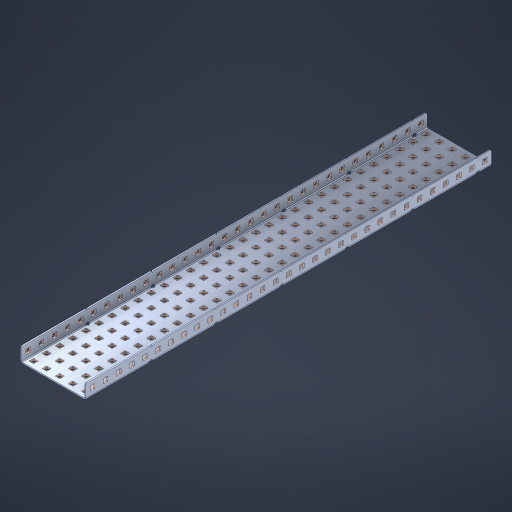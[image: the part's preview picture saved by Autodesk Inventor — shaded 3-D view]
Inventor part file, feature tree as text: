
AUTODESK INVENTOR PART (.ipt)
format: ipt  version: 2023 (Build 270158000, 158)  size: 2,308,096 bytes
history: native  units: in
note: dims shown in document units (in); Inventor stores cm internally (conversion verified against a paired STEP export)
features: other x222, extrude x216, sheet_metal_op x10, sketch x8, mirror x1, pattern_linear x1, chamfer x1
ambient origin geometry x8: Origin, YZ Plane, XZ Plane, XY Plane, X Axis, Y Axis, Z Axis, Center Point
bodies: Solid1 (feature_tree), Body (feature_tree)
feature tree (459):
  other  "Flange Pattern Plane"
  sheet_metal_op  "Flange Pattern"
  sheet_metal_op  "Body Pattern"
  other  "Arc Length"
  mirror  "Notch Mirror"
  pattern_linear  "Notch Pattern"  Spacing1=0.1875in  [1 undecoded]
  chamfer  "End Chamfer"
  extrude  "Half Cut"  Depth=0.0469in
  sketch  "Sketch1"  dims[d0=2.5in]
  other  "Plate1"
  sketch  "Sketch2"  dims[d1=15.5in]
  other  "Plate2"
  sheet_metal_op  "Bend1"
  sheet_metal_op  "Corner1"
  sketch  "Sketch3"  dims[d2=0.0469in]
  other  "Flange Pattern Sketch"
  sketch  "Sketch7"  dims[d3=0.0469in]
  other  "Srf1"
  other  "Srf2"
  sketch  "Sketch8"  dims[d4=0.0234in]
  sketch  "Sketch9"  dims[d5=0.0938in]
  other  "Srf91"
  sheet_metal_op  "Body Pattern Sketch"
  other  "Srf92"
  sketch  "Sketch13"  dims[d6=0.0469in]
  sketch  "Sketch14"  dims[d7=0.5in d8=90.0deg d9=0.0312in d10=0.1875in d11=0.0469in d12=0.0469in d16=0.182in d17=0.02in d18=0.0469in d19=0.0in d20=0.25in d21=0.25in d46=0.172in d47=1.0in d48=0.0in d49=0.182in d50=0.02in d51=0.25in d52=0.25in d53=0.0469in d54=0.0in d55=0.172in d56=1.0in d57=0.0in d60=12.2047in d62=0.5in d63=1.9685in d65=0.5in d85=0.1227in d86=0.1659in d88=0.04in d89=0.0469in d90=0.0in d91=0.04in d92=0.0491in d95=2.5in d96=0.04in d97=0.25in d98=45.0deg d101=0.0in d102=2.497in d131=2.5in d132=12.2047in d134=0.5in d139=0.5in]
  other  "Srf856"
  other  "Srf1310"
  other  "Srf1311"
  other  "Srf1312"
  other  "Srf1376"
  other  "Srf1377"
  other  "Srf1728"
  other  "Srf1755"
  other  "Srf1878"
  other  "Srf1879"
  other  "Srf1880"
  other  "Srf1881"
  other  "Srf1882"
  other  "Srf1883"
  other  "Srf1884"
  other  "Srf1885"
  other  "Srf1886"
  other  "Srf1887"
  other  "Srf1888"
  other  "Srf1889"
  other  "Srf1890"
  other  "Srf1891"
  other  "Srf1892"
  other  "Srf1893"
  other  "Srf1894"
  other  "Srf1895"
  other  "Srf1896"
  other  "Srf1897"
  other  "Srf1898"
  other  "Srf1899"
  other  "Srf1900"
  other  "Srf1901"
  other  "Srf1902"
  other  "Srf1903"
  other  "Srf1904"
  other  "Srf1905"
  other  "Srf1906"
  other  "Srf1942"
  other  "Srf1943"
  other  "Srf1944"
  other  "Srf1945"
  other  "Srf1946"
  other  "Srf1947"
  other  "Srf1948"
  other  "Srf1949"
  other  "Srf1950"
  other  "Srf1951"
  other  "Srf1952"
  other  "Srf1953"
  other  "Srf1954"
  other  "Srf1955"
  other  "Srf1956"
  other  "Srf1957"
  other  "Srf1958"
  other  "Srf1959"
  other  "Srf1960"
  other  "Srf1961"
  other  "Srf1962"
  other  "Srf1963"
  other  "Srf1964"
  other  "Srf1965"
  other  "Srf1966"
  other  "Srf1967"
  other  "Srf1968"
  other  "Srf1969"
  other  "Srf1970"
  other  "Srf2111"
  other  "Srf2112"
  other  "Srf2113"
  other  "Srf2114"
  other  "Srf2115"
  other  "Srf2116"
  other  "Srf2117"
  other  "Srf2118"
  other  "Srf2119"
  other  "Srf2120"
  other  "Srf2121"
  other  "Srf2122"
  other  "Srf2123"
  other  "Srf2124"
  other  "Srf2125"
  other  "Srf2126"
  other  "Srf2127"
  other  "Srf2128"
  other  "Srf2129"
  other  "Srf2130"
  other  "Srf2131"
  other  "Srf2132"
  other  "Srf2133"
  other  "Srf2134"
  other  "Srf2135"
  other  "Srf2136"
  other  "Srf2137"
  other  "Srf2146"
  other  "Srf2147"
  other  "Srf2148"
  other  "Srf2149"
  other  "Srf2150"
  other  "Srf2151"
  other  "Srf2152"
  other  "Srf2153"
  other  "Srf2154"
  other  "Srf2155"
  other  "Srf2156"
  other  "Srf2157"
  other  "Srf2158"
  other  "Srf2159"
  other  "Srf2160"
  other  "Srf2161"
  other  "Srf2162"
  other  "Srf2163"
  other  "Srf2164"
  other  "Srf2165"
  other  "Srf2166"
  other  "Srf2167"
  other  "Srf2168"
  other  "Srf2169"
  other  "Srf2170"
  other  "Srf2171"
  other  "Srf2172"
  other  "Srf2173"
  other  "Srf2174"
  other  "Srf2175"
  other  "Srf2176"
  other  "Srf2177"
  other  "Srf2178"
  other  "Srf2179"
  other  "Srf2180"
  other  "Srf2181"
  other  "Srf2182"
  other  "Srf2183"
  other  "Srf2184"
  other  "Srf2185"
  other  "Srf2186"
  other  "Srf2187"
  other  "Srf2188"
  other  "Srf2189"
  other  "Srf2190"
  other  "Srf2191"
  other  "Srf2192"
  other  "Srf2193"
  other  "Srf2194"
  other  "Srf2195"
  other  "Srf2196"
  other  "Srf2197"
  other  "Srf2198"
  other  "Srf2199"
  other  "Srf2200"
  other  "Srf2201"
  other  "Srf2202"
  other  "Srf2203"
  other  "Srf2204"
  other  "Srf2205"
  other  "Srf2206"
  other  "Srf2207"
  other  "Srf2208"
  other  "Srf2209"
  other  "Srf2210"
  other  "Srf2211"
  other  "Srf2212"
  other  "Srf2213"
  other  "Srf2214"
  other  "Srf2215"
  other  "Srf2216"
  other  "Srf2217"
  other  "Srf2218"
  other  "Srf2219"
  other  "Srf2220"
  other  "Srf2221"
  other  "Srf2222"
  other  "Srf2223"
  other  "Srf2224"
  other  "Srf2225"
  other  "Srf2226"
  other  "Srf2227"
  other  "Srf2228"
  other  "Srf2229"
  other  "Srf2230"
  other  "Srf2231"
  other  "Srf2232"
  other  "Srf2233"
  other  "Srf2234"
  other  "Srf2235"
  other  "Srf2236"
  other  "Srf2237"
  other  "Srf2238"
  other  "Srf2239"
  other  "Srf2240"
  other  "Srf2241"
  other  "Srf2242"
  other  "Srf2243"
  other  "Srf2244"
  other  "Srf2245"
  other  "Srf2246"
  other  "Srf2247"
  other  "Srf2248"
  other  "Srf2249"
  other  "Srf2250"
  other  "Srf2251"
  other  "Srf2252"
  other  "Srf2253"
  other  "Srf2254"
  other  "Srf2255"
  other  "Srf2256"
  other  "Srf2257"
  other  "Srf2258"
  other  "Srf2259"
  other  "Srf2260"
  other  "Srf2261"
  other  "Srf2262"
  other  "Srf2263"
  other  "Srf2264"
  other  "Srf2265"
  sheet_metal_op  "Flange Stamp"
  sheet_metal_op  "Flange Circle"
  sheet_metal_op  "Body Stamp"
  sheet_metal_op  "Body Circle"
  sheet_metal_op  "Notch"
  extrude  "ExtrusionSrf2"  Depth=0.0469in
  extrude  "ExtrusionSrf92"  Depth=2.5in
  extrude  "ExtrusionSrf856"  Depth=0.02in
  extrude  "ExtrusionSrf1310"  Depth=0.0469in
  extrude  "ExtrusionSrf1311"  TaperAngle=0.0deg  [1 undecoded]
  extrude  "ExtrusionSrf1312"  Depth=0.25in
  extrude  "ExtrusionSrf1376"  Depth=0.25in
  extrude  "ExtrusionSrf1377"  Depth=2.5in
  extrude  "ExtrusionSrf1728"  Depth=2.5in TaperAngle=0.0deg
  extrude  "ExtrusionSrf1755"  Depth=2.5in
  extrude  "ExtrusionSrf1878"  Depth=0.02in
  extrude  "ExtrusionSrf1879"  Depth=0.25in
  extrude  "ExtrusionSrf1880"  Depth=0.25in
  extrude  "ExtrusionSrf1881"  Depth=0.0469in
  extrude  "ExtrusionSrf1882"  TaperAngle=0.0deg  [1 undecoded]
  extrude  "ExtrusionSrf1883"  Depth=2.5in
  extrude  "ExtrusionSrf1884"  Depth=2.5in TaperAngle=0.0deg
  extrude  "ExtrusionSrf1885"  Depth=2.5in
  extrude  "ExtrusionSrf1886"  Depth=2.5in
  extrude  "ExtrusionSrf1887"  Depth=2.5in
  extrude  "ExtrusionSrf1888"  Depth=2.5in
  extrude  "ExtrusionSrf1889"  Depth=2.5in
  extrude  "ExtrusionSrf1890"  Depth=0.0469in
  extrude  "ExtrusionSrf1891"  TaperAngle=0.0deg  [1 undecoded]
  extrude  "ExtrusionSrf1892"  Depth=2.5in
  extrude  "ExtrusionSrf1893"  Depth=2.5in
  extrude  "ExtrusionSrf1894"  Depth=2.5in
  extrude  "ExtrusionSrf1895"  Depth=0.25in TaperAngle=45.0deg
  extrude  "ExtrusionSrf1896"  TaperAngle=0.0deg  [1 undecoded]
  extrude  "ExtrusionSrf1897"  Depth=2.5in
  extrude  "ExtrusionSrf1898"  Depth=2.5in
  extrude  "ExtrusionSrf1899"  Depth=2.5in
  extrude  "ExtrusionSrf1900"  Depth=2.5in
  extrude  "ExtrusionSrf1901"  Depth=2.5in
  extrude  "ExtrusionSrf1902"  [1 undecoded]
  extrude  "ExtrusionSrf1903"  [1 undecoded]
  extrude  "ExtrusionSrf1904"  [1 undecoded]
  extrude  "ExtrusionSrf1905"  [1 undecoded]
  extrude  "ExtrusionSrf1906"  [1 undecoded]
  extrude  "ExtrusionSrf1942"  [1 undecoded]
  extrude  "ExtrusionSrf1943"  [1 undecoded]
  extrude  "ExtrusionSrf1944"  [1 undecoded]
  extrude  "ExtrusionSrf1945"  [1 undecoded]
  extrude  "ExtrusionSrf1946"  [1 undecoded]
  extrude  "ExtrusionSrf1947"  [1 undecoded]
  extrude  "ExtrusionSrf1948"  [1 undecoded]
  extrude  "ExtrusionSrf1949"  [1 undecoded]
  extrude  "ExtrusionSrf1950"  [1 undecoded]
  extrude  "ExtrusionSrf1951"  [1 undecoded]
  extrude  "ExtrusionSrf1952"  [1 undecoded]
  extrude  "ExtrusionSrf1953"  [1 undecoded]
  extrude  "ExtrusionSrf1954"  [1 undecoded]
  extrude  "ExtrusionSrf1955"  [1 undecoded]
  extrude  "ExtrusionSrf1956"  [1 undecoded]
  extrude  "ExtrusionSrf1957"  [1 undecoded]
  extrude  "ExtrusionSrf1958"  [1 undecoded]
  extrude  "ExtrusionSrf1959"  [1 undecoded]
  extrude  "ExtrusionSrf1960"  [1 undecoded]
  extrude  "ExtrusionSrf1961"  [1 undecoded]
  extrude  "ExtrusionSrf1962"  [1 undecoded]
  extrude  "ExtrusionSrf1963"  [1 undecoded]
  extrude  "ExtrusionSrf1964"  [1 undecoded]
  extrude  "ExtrusionSrf1965"  [1 undecoded]
  extrude  "ExtrusionSrf1966"  [1 undecoded]
  extrude  "ExtrusionSrf1967"  [1 undecoded]
  extrude  "ExtrusionSrf1968"  [1 undecoded]
  extrude  "ExtrusionSrf1969"  [1 undecoded]
  extrude  "ExtrusionSrf1970"  [1 undecoded]
  extrude  "ExtrusionSrf2111"  [1 undecoded]
  extrude  "ExtrusionSrf2112"  [1 undecoded]
  extrude  "ExtrusionSrf2113"  [1 undecoded]
  extrude  "ExtrusionSrf2114"  [1 undecoded]
  extrude  "ExtrusionSrf2115"  [1 undecoded]
  extrude  "ExtrusionSrf2116"  [1 undecoded]
  extrude  "ExtrusionSrf2117"  [1 undecoded]
  extrude  "ExtrusionSrf2118"  [1 undecoded]
  extrude  "ExtrusionSrf2119"  [1 undecoded]
  extrude  "ExtrusionSrf2120"  [1 undecoded]
  extrude  "ExtrusionSrf2121"  [1 undecoded]
  extrude  "ExtrusionSrf2122"  [1 undecoded]
  extrude  "ExtrusionSrf2123"  [1 undecoded]
  extrude  "ExtrusionSrf2124"  [1 undecoded]
  extrude  "ExtrusionSrf2125"  [1 undecoded]
  extrude  "ExtrusionSrf2126"  [1 undecoded]
  extrude  "ExtrusionSrf2127"  [1 undecoded]
  extrude  "ExtrusionSrf2128"  [1 undecoded]
  extrude  "ExtrusionSrf2129"  [1 undecoded]
  extrude  "ExtrusionSrf2130"  [1 undecoded]
  extrude  "ExtrusionSrf2131"  [1 undecoded]
  extrude  "ExtrusionSrf2132"  [1 undecoded]
  extrude  "ExtrusionSrf2133"  [1 undecoded]
  extrude  "ExtrusionSrf2134"  [1 undecoded]
  extrude  "ExtrusionSrf2135"  [1 undecoded]
  extrude  "ExtrusionSrf2136"  [1 undecoded]
  extrude  "ExtrusionSrf2137"  [1 undecoded]
  extrude  "ExtrusionSrf2146"  [1 undecoded]
  extrude  "ExtrusionSrf2147"  [1 undecoded]
  extrude  "ExtrusionSrf2148"  [1 undecoded]
  extrude  "ExtrusionSrf2149"  [1 undecoded]
  extrude  "ExtrusionSrf2150"  [1 undecoded]
  extrude  "ExtrusionSrf2151"  [1 undecoded]
  extrude  "ExtrusionSrf2152"  [1 undecoded]
  extrude  "ExtrusionSrf2153"  [1 undecoded]
  extrude  "ExtrusionSrf2154"  [1 undecoded]
  extrude  "ExtrusionSrf2155"  [1 undecoded]
  extrude  "ExtrusionSrf2156"  [1 undecoded]
  extrude  "ExtrusionSrf2157"  [1 undecoded]
  extrude  "ExtrusionSrf2158"  [1 undecoded]
  extrude  "ExtrusionSrf2159"  [1 undecoded]
  extrude  "ExtrusionSrf2160"  [1 undecoded]
  extrude  "ExtrusionSrf2161"  [1 undecoded]
  extrude  "ExtrusionSrf2162"  [1 undecoded]
  extrude  "ExtrusionSrf2163"  [1 undecoded]
  extrude  "ExtrusionSrf2164"  [1 undecoded]
  extrude  "ExtrusionSrf2165"  [1 undecoded]
  extrude  "ExtrusionSrf2166"  [1 undecoded]
  extrude  "ExtrusionSrf2167"  [1 undecoded]
  extrude  "ExtrusionSrf2168"  [1 undecoded]
  extrude  "ExtrusionSrf2169"  [1 undecoded]
  extrude  "ExtrusionSrf2170"  [1 undecoded]
  extrude  "ExtrusionSrf2171"  [1 undecoded]
  extrude  "ExtrusionSrf2172"  [1 undecoded]
  extrude  "ExtrusionSrf2173"  [1 undecoded]
  extrude  "ExtrusionSrf2174"  [1 undecoded]
  extrude  "ExtrusionSrf2175"  [1 undecoded]
  extrude  "ExtrusionSrf2176"  [1 undecoded]
  extrude  "ExtrusionSrf2177"  [1 undecoded]
  extrude  "ExtrusionSrf2178"  [1 undecoded]
  extrude  "ExtrusionSrf2179"  [1 undecoded]
  extrude  "ExtrusionSrf2180"  [1 undecoded]
  extrude  "ExtrusionSrf2181"  [1 undecoded]
  extrude  "ExtrusionSrf2182"  [1 undecoded]
  extrude  "ExtrusionSrf2183"  [1 undecoded]
  extrude  "ExtrusionSrf2184"  [1 undecoded]
  extrude  "ExtrusionSrf2185"  [1 undecoded]
  extrude  "ExtrusionSrf2186"  [1 undecoded]
  extrude  "ExtrusionSrf2187"  [1 undecoded]
  extrude  "ExtrusionSrf2188"  [1 undecoded]
  extrude  "ExtrusionSrf2189"  [1 undecoded]
  extrude  "ExtrusionSrf2190"  [1 undecoded]
  extrude  "ExtrusionSrf2191"  [1 undecoded]
  extrude  "ExtrusionSrf2192"  [1 undecoded]
  extrude  "ExtrusionSrf2193"  [1 undecoded]
  extrude  "ExtrusionSrf2194"  [1 undecoded]
  extrude  "ExtrusionSrf2195"  [1 undecoded]
  extrude  "ExtrusionSrf2196"  [1 undecoded]
  extrude  "ExtrusionSrf2197"  [1 undecoded]
  extrude  "ExtrusionSrf2198"  [1 undecoded]
  extrude  "ExtrusionSrf2199"  [1 undecoded]
  extrude  "ExtrusionSrf2200"  [1 undecoded]
  extrude  "ExtrusionSrf2201"  [1 undecoded]
  extrude  "ExtrusionSrf2202"  [1 undecoded]
  extrude  "ExtrusionSrf2203"  [1 undecoded]
  extrude  "ExtrusionSrf2204"  [1 undecoded]
  extrude  "ExtrusionSrf2205"  [1 undecoded]
  extrude  "ExtrusionSrf2206"  [1 undecoded]
  extrude  "ExtrusionSrf2207"  [1 undecoded]
  extrude  "ExtrusionSrf2208"  [1 undecoded]
  extrude  "ExtrusionSrf2209"  [1 undecoded]
  extrude  "ExtrusionSrf2210"  [1 undecoded]
  extrude  "ExtrusionSrf2211"  [1 undecoded]
  extrude  "ExtrusionSrf2212"  [1 undecoded]
  extrude  "ExtrusionSrf2213"  [1 undecoded]
  extrude  "ExtrusionSrf2214"  [1 undecoded]
  extrude  "ExtrusionSrf2215"  [1 undecoded]
  extrude  "ExtrusionSrf2216"  [1 undecoded]
  extrude  "ExtrusionSrf2217"  [1 undecoded]
  extrude  "ExtrusionSrf2218"  [1 undecoded]
  extrude  "ExtrusionSrf2219"  [1 undecoded]
  extrude  "ExtrusionSrf2220"  [1 undecoded]
  extrude  "ExtrusionSrf2221"  [1 undecoded]
  extrude  "ExtrusionSrf2222"  [1 undecoded]
  extrude  "ExtrusionSrf2223"  [1 undecoded]
  extrude  "ExtrusionSrf2224"  [1 undecoded]
  extrude  "ExtrusionSrf2225"  [1 undecoded]
  extrude  "ExtrusionSrf2226"  [1 undecoded]
  extrude  "ExtrusionSrf2227"  [1 undecoded]
  extrude  "ExtrusionSrf2228"  [1 undecoded]
  extrude  "ExtrusionSrf2229"  [1 undecoded]
  extrude  "ExtrusionSrf2230"  [1 undecoded]
  extrude  "ExtrusionSrf2231"  [1 undecoded]
  extrude  "ExtrusionSrf2232"  [1 undecoded]
  extrude  "ExtrusionSrf2233"  [1 undecoded]
  extrude  "ExtrusionSrf2234"  [1 undecoded]
  extrude  "ExtrusionSrf2235"  [1 undecoded]
  extrude  "ExtrusionSrf2236"  [1 undecoded]
  extrude  "ExtrusionSrf2237"  [1 undecoded]
  extrude  "ExtrusionSrf2238"  [1 undecoded]
  extrude  "ExtrusionSrf2239"  [1 undecoded]
  extrude  "ExtrusionSrf2240"  [1 undecoded]
  extrude  "ExtrusionSrf2241"  [1 undecoded]
  extrude  "ExtrusionSrf2242"  [1 undecoded]
  extrude  "ExtrusionSrf2243"  [1 undecoded]
  extrude  "ExtrusionSrf2244"  [1 undecoded]
  extrude  "ExtrusionSrf2245"  [1 undecoded]
  extrude  "ExtrusionSrf2246"  [1 undecoded]
  extrude  "ExtrusionSrf2247"  [1 undecoded]
  extrude  "ExtrusionSrf2248"  [1 undecoded]
  extrude  "ExtrusionSrf2249"  [1 undecoded]
  extrude  "ExtrusionSrf2250"  [1 undecoded]
  extrude  "ExtrusionSrf2251"  [1 undecoded]
  extrude  "ExtrusionSrf2252"  [1 undecoded]
  extrude  "ExtrusionSrf2253"  [1 undecoded]
  extrude  "ExtrusionSrf2254"  [1 undecoded]
  extrude  "ExtrusionSrf2255"  [1 undecoded]
  extrude  "ExtrusionSrf2256"  [1 undecoded]
  extrude  "ExtrusionSrf2257"  [1 undecoded]
  extrude  "ExtrusionSrf2258"  [1 undecoded]
  extrude  "ExtrusionSrf2259"  [1 undecoded]
  extrude  "ExtrusionSrf2260"  [1 undecoded]
  extrude  "ExtrusionSrf2261"  [1 undecoded]
  extrude  "ExtrusionSrf2262"  [1 undecoded]
  extrude  "ExtrusionSrf2263"  [1 undecoded]
  extrude  "ExtrusionSrf2264"  [1 undecoded]
  extrude  "ExtrusionSrf2265"  [1 undecoded]
note: 186 required parameter values undecoded (feature->parameter linkage not recoverable at this tier; creation-order binding heuristic only, values carry confidence <= 0.55)
